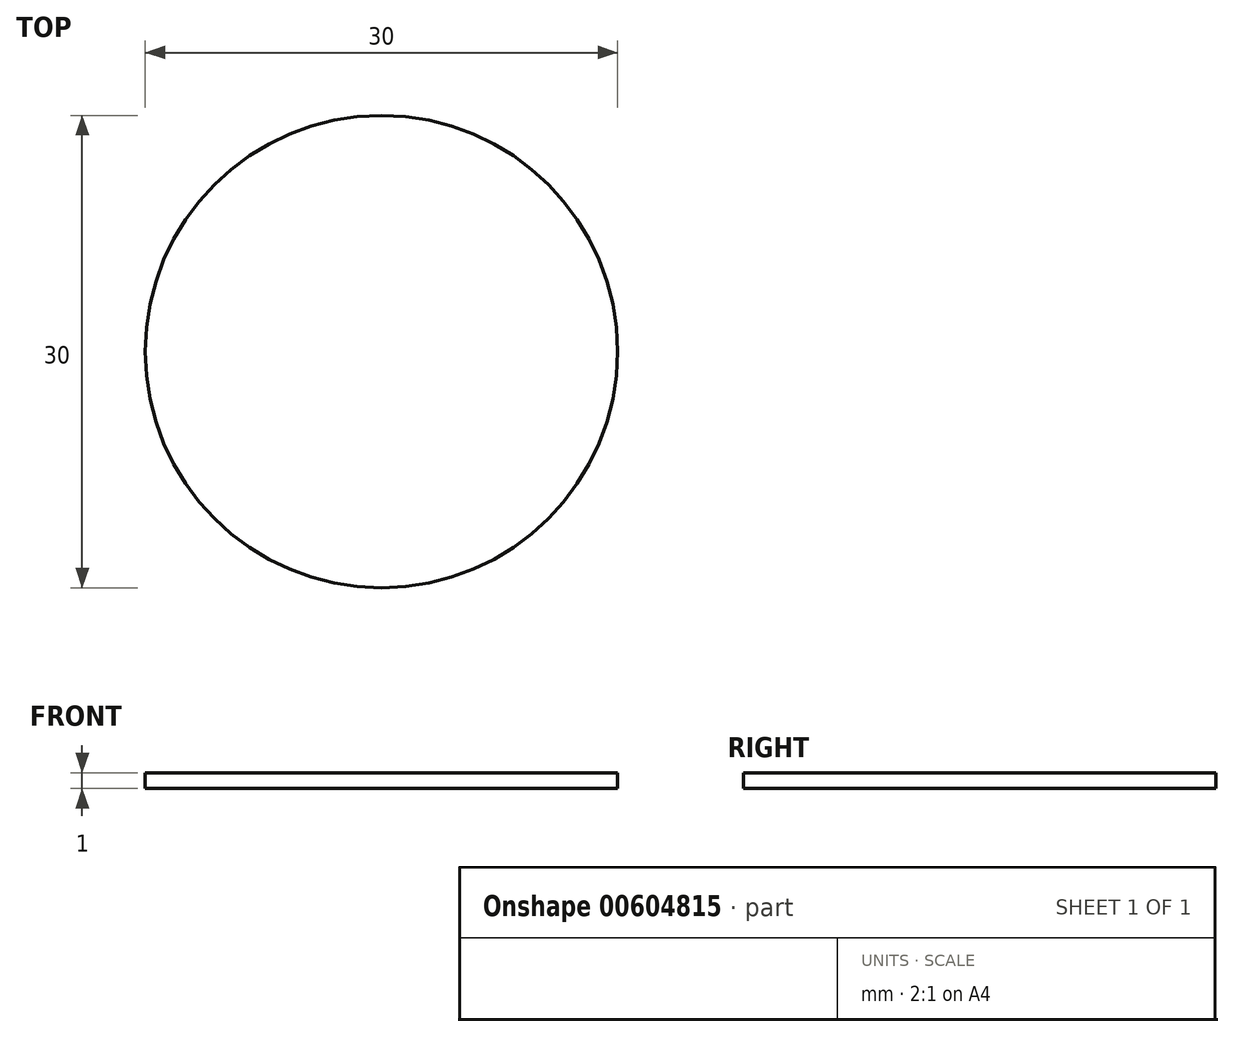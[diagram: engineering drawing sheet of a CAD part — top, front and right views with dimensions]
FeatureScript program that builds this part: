
annotation { "Feature Type Name" : "Feature", "Feature Type Description" : "" }
export const myFeature = defineFeature(function(context is Context, id is Id, definition is map)
    precondition{}
    {
        {
            var Q0;
            Q0=qCreatedBy(makeId("Top.planeOp"),FACE);
            var sketch = newSketch(context, id + "F0", { "sketchPlane" : qUnion([Q0])});
            skCircle(sketch, "E0", {"center": v(0, 0) * mm, "radius": 15 * mm});
            skSolve(sketch);
        }
        {
            var Q0;
            Q0=makeQuery(id+"F0.imprint","IMPRINT",FACE,{"disambiguationData":[TD([[makeQuery(id+"F0.imprint","IMPRINT",EDGE,{"derivedFrom":sQuery(id+"F0.wireOp",EDGE,"E0")}),1.0]])]});
            extrude(context, id + "F1", {"entities" : qUnion([Q0]), "depth" : 1 * mm, "offsetDistance" : 25.4 * mm});
        }
    });
